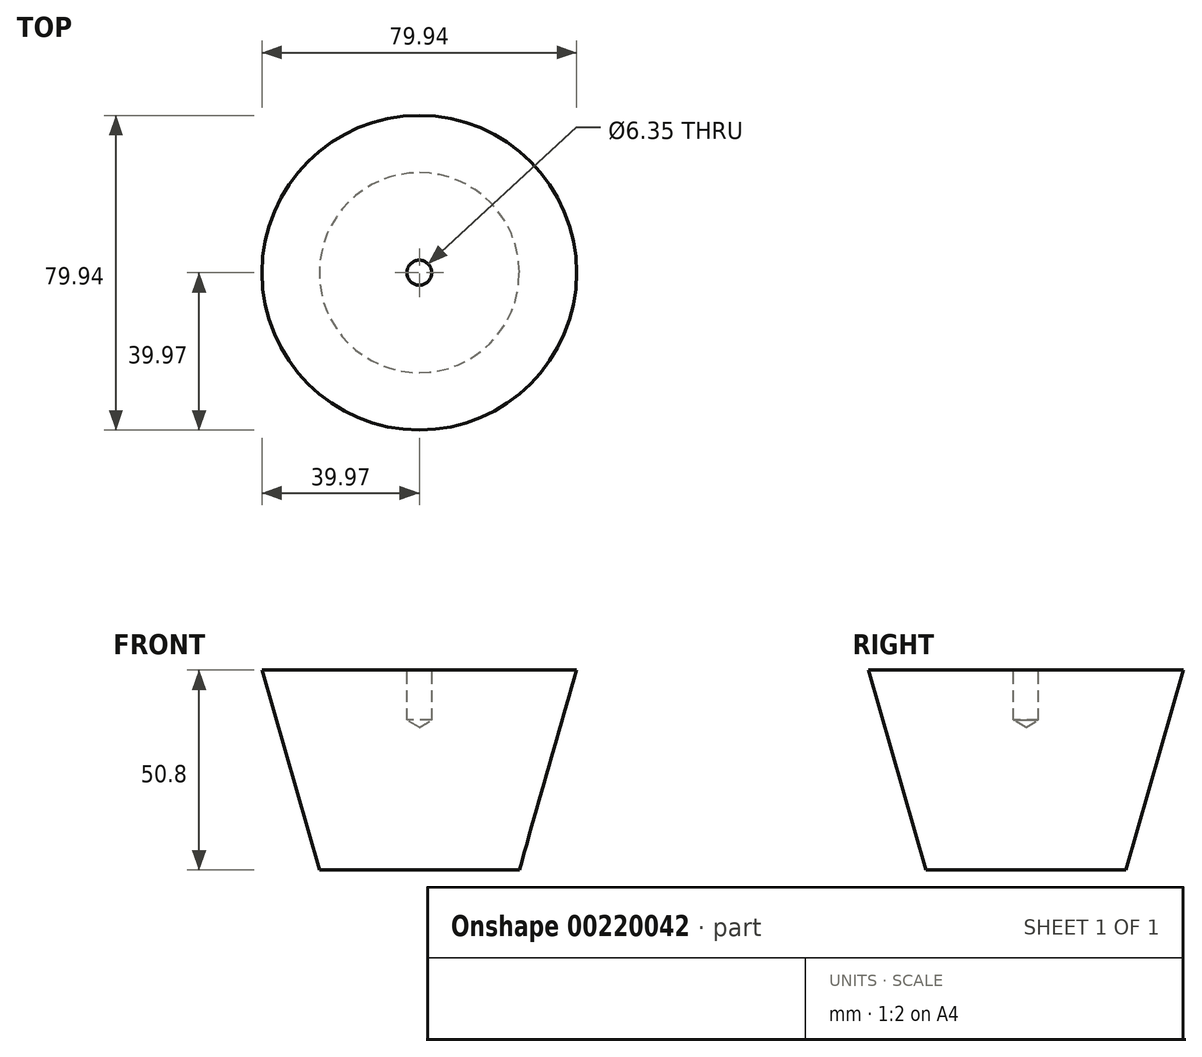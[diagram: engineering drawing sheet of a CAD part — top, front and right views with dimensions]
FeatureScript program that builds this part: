
annotation { "Feature Type Name" : "Feature", "Feature Type Description" : "" }
export const myFeature = defineFeature(function(context is Context, id is Id, definition is map)
    precondition{}
    {
        {
            var Q0;
            Q0=qCreatedBy(makeId("Top.planeOp"),FACE);
            var sketch = newSketch(context, id + "F0", { "sketchPlane" : qUnion([Q0])});
            skCircle(sketch, "E0", {"center": v(0, 0) * mm, "radius": 25.4 * mm});
            skSolve(sketch);
        }
        {
            var Q0;
            Q0=makeQuery(id+"F0.imprint","IMPRINT",FACE,{"disambiguationData":[TD([[makeQuery(id+"F0.imprint","IMPRINT",EDGE,{"derivedFrom":sQuery(id+"F0.wireOp",EDGE,"E0")}),1.0]])]});
            extrude(context, id + "F1", {"entities" : qUnion([Q0]), "depth" : 50.8 * mm, "hasDraft" : true, "draftAngle" : 16 * degree});
        }
        {
            var Q0;
            Q0=makeQuery(id+"F1.opExtrude","CAP_FACE",FACE,{"disambiguationData":[OSD([sQuery(id+"F0.wireOp",EDGE,"E0")])],"isStart":false});
            var sketch = newSketch(context, id + "F2", { "sketchPlane" : qUnion([Q0])});
            skCircle(sketch, "E1", {"center": v(0, 0) * mm, "radius": 3.18 * mm});
            skSolve(sketch);
        }
        {
            var Q0;
            Q0=sQuery(id+"F2.wireOp",VERTEX,"E1.center");
            var Q1;
            Q1=makeQuery(id+"F1.opExtrude","SWEPT_BODY",BODY,{"disambiguationData":[OSD([sQuery(id+"F0.wireOp",EDGE,"E0")])]});
            hole(context, id + "F3", {"style" : HoleStyle.SIMPLE, "endStyle" : HoleEndStyle.BLIND, "holeDiameter" : 6.35 * mm, "holeDepth" : 12.7 * mm, "locations" : qUnion([Q0]), "scope" : qUnion([Q1])});
        }
    });
